# Revit family: g2021_EN_Roll-up_Door_Ferroflex_Alumroll_D00682ES
name_source: partatom
category: Doors
units: mm (PartAtom-declared; Revit-internal decimal feet)

## family parameters
Always vertical = Yes
Cut with Voids When Loaded = No
Host = Wall
OmniClass Number = 23.30.10.00
OmniClass Title = Doors
Room Calculation Point = No
Shared = No

## types (1)
- Roll-up Door 4000 x 4000 mm
    A = 224 mm  [stored 0.734908 ft]
    Analytic Construction = <Ninguno>
    Article Number = D00682ES-V2
    Assembly Place = On site
    Atmospheric Acidification Per Unit = 0
    B = 205 mm
    BIM Content Download Platform = www.bimetica.com
    BIM Eelement Expiry Date = 2 years
    BIM Element Issue Date = 16/12/2022
    BIM Profile URL = https://bimetica.com
    BIM technical support = https://bimsupport.info
    C = 480 mm  [stored 1.5748 ft]
    CE Mark = Yes
    COBie Category = IfcDoor
    Clear Area to Access = 0 mm  [stored 0 ft]
    Clear Height = 4000 mm  [stored 13.1234 ft]
    Clear Width = 4000 mm  [stored 13.1234 ft]
    Climate Change Per Unit = 0
    Code = Alumroll
    Container Material = Wooden box
    Control panel Height = 1200 mm
    Curtain Material = PVC_Blue
    D = 130 mm
    Declaration of Performance URL = https://ferroflexindustrialaccess.com
    Define Thermal Properties by = Schematic Type
    Description = Rapid roll-up door, consisting of guides and head in lacquered or anodized aluminum. PVC canvas with polyester fabric, color to choose. Control panel with variator. Active security by means of crossed photocells barriers and possibility of lower skirt with resistive band.
    E = 73 mm  [stored 0.239501 ft]
    Energy Spent = 0
    Eutrophication Per Unit = 0
    Exterior Offset = 0 mm  [stored 0 ft]
    Finish = Lacquered
    Fire Rating = Canvas ISO 3795-89
    FireExit = No
    Frame Projection Ext. = 200 mm
    Frame Projection Int. = 100 mm  [stored 0.328084 ft]
    Function = Exterior
    G = 300 mm
    GDO-BIM Standard Version = GDO-BIM V02
    Glazing Area Fraction = 0
    Gubimclass Code = Puertas de acceso
    Gubimclass Title = 80.10.40.20
    H = 430 mm
    HasDrive = Yes
    Hazardous Waste Per Unit = 0
    Height = 4000 mm  [stored 13.1234 ft]
    History = (RVT2021) Creation of Element.
    IfcExportAs = IfcDoor
    IfcExportType = Roll-up door
    Inert Waste Per Unit = 0
    Infiltration = 0
    Interior Offset = 0 mm  [stored 0 ft]
    Is Accesible = No
    Is Extended Warranty = No
    Is External = Yes
    License Number = XXX-XXXX7125
    Maintenance Cost = 0
    Manufacturer = Ferroflex S.L.U.
    Masterformat Code = 08 31 00
    Masterformat Title = Access Doors and Panels
    Material = Aluminium_Laquered
    Measuring Unit = Unit
    Minimum Required Height = 2100 mm
    Model = Alumroll
    Model Label = Alumroll Roll-up Door
    Non Renewable Energy Consumption Per Unit = 0
    NonHazardous Waste Per Unit = 0
    Omniclass Code = 23-17 11 27 13
    Omniclass Title = Access Doors
    Operation = Enrrollable
    Photochemical Ozone Formation Per Unit = 0
    Product URL = https://ferroflexindustrialaccess.com
    Radioactive Waste Per Unit = 0
    Reference = D00682ES-V2
    Renewable Energy Consumption Per Unit = 0
    Resource Depletion Per Unit = 0
    Safety Standard = 2006/42/CE
    Security Rating = ISO 1421 / ISO 13937-2
    Self Closing = No
    Series = Roll-up Doors
    Sight glass area = Possibility of sight glass areas are available
    SmokeStop = No
    Stratospheric Ozone Layer Destruction Per Unit = 0
    Thickness = 73 mm  [stored 0.239501 ft]
    Total Primary Energy Consumption Per Unit = 0
    UNSPSC Code = 30171503
    UNSPSC Title = Rolling doors
    URL = https://ferroflexindustrialaccess.com
https://ferroflexindustrialaccess.com
    Version = RVT2021
    Wall Closure = Interior
    Warranty Content = Materials
    Warranty Period = One year
    Water Consumption Per Unit = 0
    Weight = 0.00 kg
    Width = 4000 mm  [stored 13.1234 ft]
    Wind Load Rating = Class 2
    Wrapping Material = Plastic wrapping

note: [stored X ft] marks values corroborated as IEEE doubles in the binary element streams (Revit-internal decimal feet)

## geometry (parser evidence)
native form markers: Sweep x2
no freeform markers — native parametric forms only
